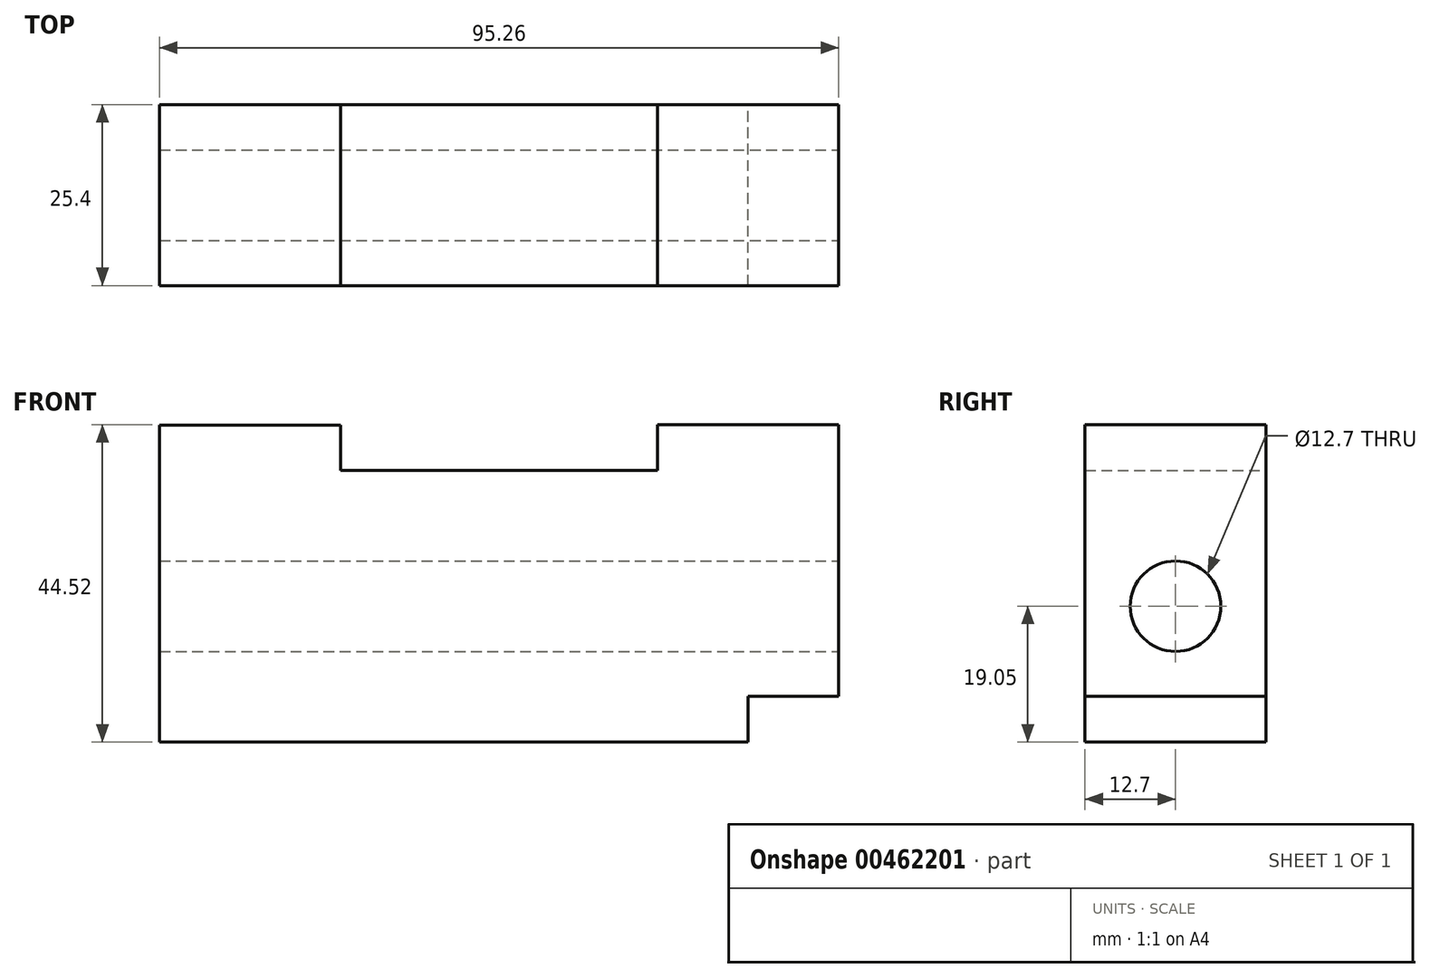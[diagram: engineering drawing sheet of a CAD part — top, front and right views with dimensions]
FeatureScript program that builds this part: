
annotation { "Feature Type Name" : "Feature", "Feature Type Description" : "" }
export const myFeature = defineFeature(function(context is Context, id is Id, definition is map)
    precondition{}
    {
        {
            var Q0;
            Q0=qCreatedBy(makeId("Front.planeOp"),FACE);
            var sketch = newSketch(context, id + "F0", { "sketchPlane" : qUnion([Q0])});
            skLineSegment(sketch, "E0.bottom", {"start": v(-41.28, -19.05) * mm, "end": v(41.28, -19.05) * mm});
            skLineSegment(sketch, "E0.top", {"start": v(-41.28, 19.05) * mm, "end": v(41.28, 19.05) * mm});
            skLineSegment(sketch, "E0.left", {"start": v(-41.27, -19.05) * mm, "end": v(-41.28, 19.05) * mm});
            skLineSegment(sketch, "E0.right", {"start": v(41.28, -19.05) * mm, "end": v(41.28, 19.05) * mm});
            skPoint(sketch, "E0.middle", {"position": v(0, 0) * mm});
            skSolve(sketch);
        }
        {
            var Q0;
            Q0=makeQuery(id+"F0.imprint","IMPRINT",FACE,{"disambiguationData":[TD([[makeQuery(id+"F0.imprint","IMPRINT",EDGE,{"derivedFrom":sQuery(id+"F0.wireOp",EDGE,"E0.bottom")}),1.0]])]});
            var sketch = newSketch(context, id + "F1", { "sketchPlane" : qUnion([Q0])});
            skSolve(sketch);
        }
        {
            var Q0;
            Q0 = qSketchRegion(id + "F1", true);
            var Q1;
            Q1=makeQuery(id+"F0.imprint","IMPRINT",FACE,{"disambiguationData":[TD([[makeQuery(id+"F0.imprint","IMPRINT",EDGE,{"derivedFrom":sQuery(id+"F0.wireOp",EDGE,"E0.bottom")}),1.0]])]});
            extrude(context, id + "F2", {"entities" : qUnion([Q0, Q1]), "endBound" : BoundingType.SYMMETRIC, "depth" : 25.4 * mm});
        }
        {
            var Q0;
            Q0=makeQuery(id+"F2.opExtrude","SWEPT_FACE",FACE,{"disambiguationData":[OSD([sQuery(id+"F0.wireOp",EDGE,"E0.top")])]});
            var sketch = newSketch(context, id + "F3", { "sketchPlane" : qUnion([Q0])});
            skLineSegment(sketch, "E1.bottom", {"start": v(-41.28, 12.7) * mm, "end": v(-15.88, 12.7) * mm});
            skLineSegment(sketch, "E1.top", {"start": v(-41.28, -12.7) * mm, "end": v(-15.88, -12.7) * mm});
            skLineSegment(sketch, "E1.left", {"start": v(-41.28, 12.7) * mm, "end": v(-41.28, -12.7) * mm});
            skLineSegment(sketch, "E1.right", {"start": v(-15.88, 12.7) * mm, "end": v(-15.88, -12.7) * mm});
            skSolve(sketch);
        }
        {
            var Q0;
            Q0=makeQuery(id+"F3.imprint","IMPRINT",FACE,{"disambiguationData":[TD([[makeQuery(id+"F3.imprint","IMPRINT",EDGE,{"derivedFrom":sQuery(id+"F3.wireOp",EDGE,"E1.bottom")}),-1.0]])]});
            extrude(context, id + "F4", {"entities" : qUnion([Q0]), "operationType" : NewBodyOperationType.ADD, "endBound" : BoundingType.SYMMETRIC, "depth" : 12.7 * mm});
        }
        {
            var Q0;
            Q0=makeQuery(id+"F2.opExtrude","SWEPT_FACE",FACE,{"disambiguationData":[OSD([sQuery(id+"F0.wireOp",EDGE,"E0.right")])]});
            var sketch = newSketch(context, id + "F5", { "sketchPlane" : qUnion([Q0])});
            skLineSegment(sketch, "E2.bottom", {"start": v(-12.7, -12.63) * mm, "end": v(12.7, -12.63) * mm});
            skLineSegment(sketch, "E2.top", {"start": v(-12.7, 25.47) * mm, "end": v(12.7, 25.47) * mm});
            skLineSegment(sketch, "E2.left", {"start": v(-12.7, -12.63) * mm, "end": v(-12.7, 25.47) * mm});
            skLineSegment(sketch, "E2.right", {"start": v(12.7, -12.63) * mm, "end": v(12.7, 25.47) * mm});
            skSolve(sketch);
        }
        {
            var Q0;
            {var subQ0=sQuery(id+"F5.wireOp",EDGE,"E2.top");Q0=makeQuery(id+"F5.imprint","IMPRINT",FACE,{"disambiguationData":[TD([[makeQuery(id+"F5.imprint","IMPRINT",EDGE,{"derivedFrom":subQ0}),-1.0]])]});}
            var Q1;
            {var subQ0=sQuery(id+"F5.wireOp",EDGE,"E2.bottom");Q1=makeQuery(id+"F5.imprint","IMPRINT",FACE,{"disambiguationData":[TD([[makeQuery(id+"F5.imprint","IMPRINT",EDGE,{"derivedFrom":subQ0}),1.0]])]});}
            extrude(context, id + "F6", {"entities" : qUnion([Q0, Q1]), "operationType" : NewBodyOperationType.ADD, "endBound" : BoundingType.SYMMETRIC, "depth" : 25.4 * mm});
        }
        {
            var Q0;
            Q0=makeQuery(id+"F6.opExtrude","CAP_FACE",FACE,{"disambiguationData":[OSD([sQuery(id+"F5.wireOp",EDGE,"E2.bottom"),sQuery(id+"F5.wireOp",EDGE,"E2.top"),sQuery(id+"F5.wireOp",EDGE,"E2.left"),sQuery(id+"F5.wireOp",EDGE,"E2.right")])],"isStart":false});
            var sketch = newSketch(context, id + "F7", { "sketchPlane" : qUnion([Q0])});
            skCircle(sketch, "E3", {"center": v(0, 0) * mm, "radius": 6.35 * mm});
            skSolve(sketch);
        }
        {
            var Q0;
            Q0=makeQuery(id+"F7.imprint","IMPRINT",FACE,{"disambiguationData":[TD([[makeQuery(id+"F7.imprint","IMPRINT",EDGE,{"derivedFrom":sQuery(id+"F7.wireOp",EDGE,"E3")}),1.0]])]});
            extrude(context, id + "F8", {"entities" : qUnion([Q0]), "operationType" : NewBodyOperationType.REMOVE, "endBound" : BoundingType.THROUGH_ALL, "oppositeDirection" : true, "depth" : 25.4 * mm});
        }
    });
